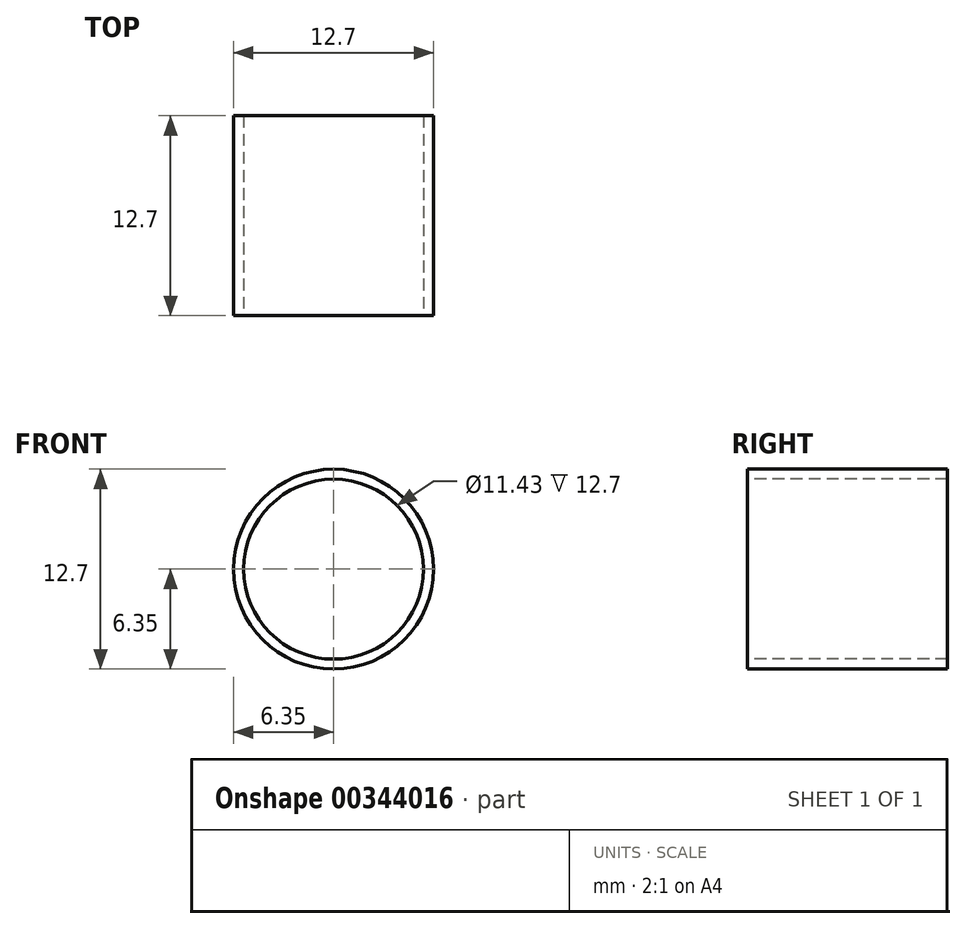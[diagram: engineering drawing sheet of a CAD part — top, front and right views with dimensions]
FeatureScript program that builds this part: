
annotation { "Feature Type Name" : "Feature", "Feature Type Description" : "" }
export const myFeature = defineFeature(function(context is Context, id is Id, definition is map)
    precondition{}
    {
        {
            var Q0;
            Q0=qCreatedBy(makeId("Front.planeOp"),FACE);
            var sketch = newSketch(context, id + "F0", { "sketchPlane" : qUnion([Q0])});
            skCircle(sketch, "E0", {"center": v(0, 0) * mm, "radius": 6.35 * mm});
            skCircle(sketch, "E1", {"center": v(0, 0) * mm, "radius": 5.72 * mm});
            skSolve(sketch);
        }
        {
            var Q0;
            Q0 = qSketchRegion(id + "F0", true);
            extrude(context, id + "F1", {"entities" : qUnion([Q0]), "oppositeDirection" : true, "depth" : 12.7 * mm});
        }
    });
